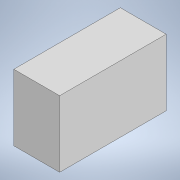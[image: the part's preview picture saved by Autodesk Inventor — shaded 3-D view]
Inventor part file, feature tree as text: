
AUTODESK INVENTOR PART (.ipt)
format: ipt  version: 2020 (Build 240168000, 168)  size: 84,480 bytes
history: native  units: mm
features: other x1, extrude x1, sketch x1
ambient origin geometry x8: Origin, YZ Plane, XZ Plane, XY Plane, X Axis, Y Axis, Z Axis, Center Point
bodies: Body1 (feature_tree)
feature tree (3):
  other  "솔리드1"
  extrude  "돌출1"  Depth=65.0mm
  sketch  "스케치1"
